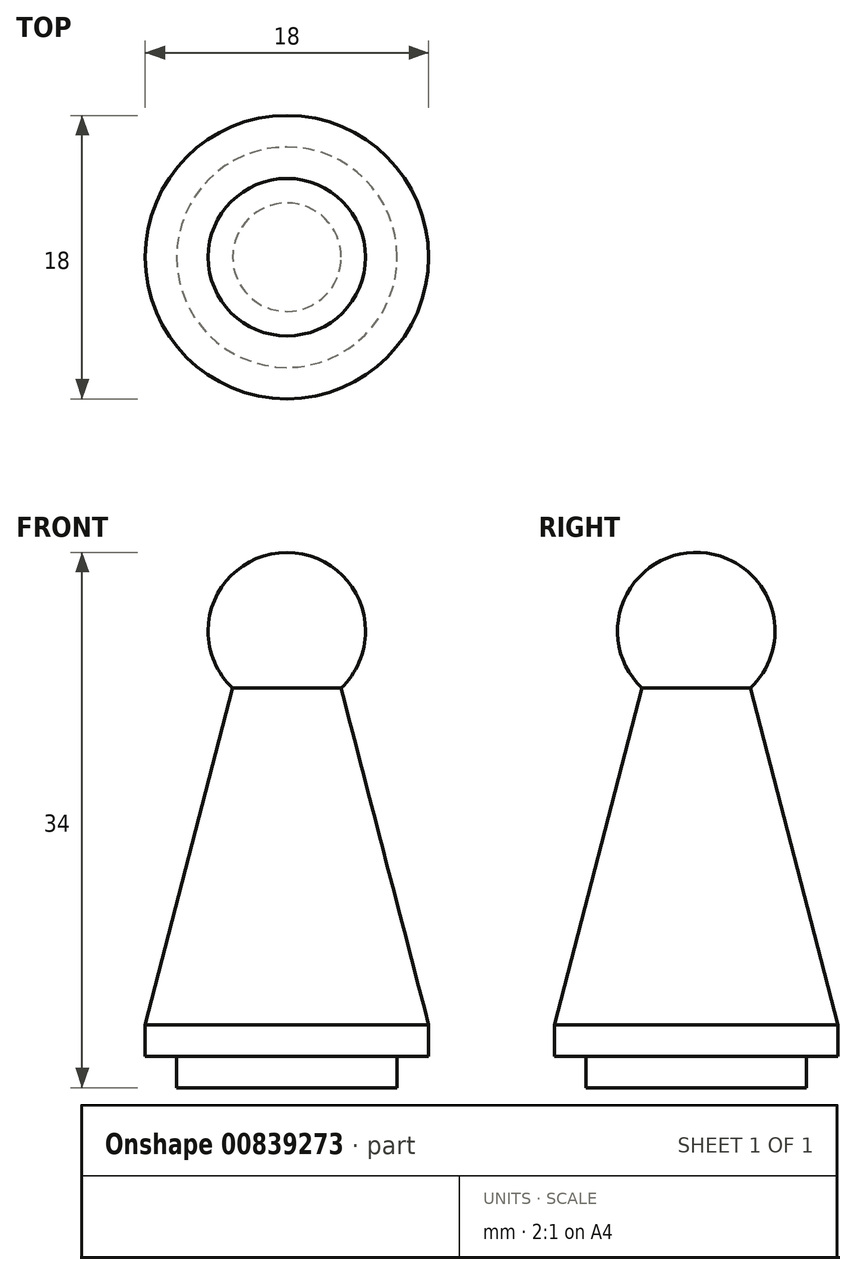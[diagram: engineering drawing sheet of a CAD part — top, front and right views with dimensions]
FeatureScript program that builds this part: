
annotation { "Feature Type Name" : "Feature", "Feature Type Description" : "" }
export const myFeature = defineFeature(function(context is Context, id is Id, definition is map)
    precondition{}
    {
        {
            var Q0;
            Q0=qCreatedBy(makeId("Top.planeOp"),FACE);
            var sketch = newSketch(context, id + "F0", { "sketchPlane" : qUnion([Q0])});
            skCircle(sketch, "E0", {"center": v(0, 0) * mm, "radius": 7 * mm});
            skSolve(sketch);
        }
        {
            var Q0;
            Q0=makeQuery(id+"F0.imprint","IMPRINT",FACE,{"disambiguationData":[TD([[makeQuery(id+"F0.imprint","IMPRINT",EDGE,{"derivedFrom":sQuery(id+"F0.wireOp",EDGE,"E0")}),1.0]])]});
            extrude(context, id + "F1", {"entities" : qUnion([Q0]), "depth" : 2 * mm, "offsetDistance" : 25 * mm});
        }
        {
            var Q0;
            Q0=makeQuery(id+"F1.opExtrude","CAP_FACE",FACE,{"disambiguationData":[OSD([sQuery(id+"F0.wireOp",EDGE,"E0")])],"isStart":false});
            var sketch = newSketch(context, id + "F2", { "sketchPlane" : qUnion([Q0])});
            skCircle(sketch, "E1", {"center": v(0, 0) * mm, "radius": 9 * mm});
            skSolve(sketch);
        }
        {
            var Q0;
            Q0 = qSketchRegion(id + "F2", true);
            extrude(context, id + "F3", {"entities" : qUnion([Q0]), "operationType" : NewBodyOperationType.ADD, "depth" : 2 * mm, "offsetDistance" : 25 * mm});
        }
        {
            var Q0;
            Q0=makeQuery(id+"F3.opExtrude","CAP_FACE",FACE,{"disambiguationData":[OSD([sQuery(id+"F2.wireOp",EDGE,"E1")])],"isStart":false});
            cPlane(context, id + "F4", {"entities" : qUnion([Q0]), "cplaneType" : CPlaneType.OFFSET, "offset" : 25 * mm, "width" : 150 * mm, "height" : 150 * mm});
        }
        {
            var Q0;
            Q0=qCreatedBy(id+"F4.planeOp",FACE);
            var sketch = newSketch(context, id + "F5", { "sketchPlane" : qUnion([Q0])});
            skCircle(sketch, "E2", {"center": v(0, 0) * mm, "radius": 2.5 * mm});
            skSolve(sketch);
        }
        {
            var Q1;
            Q1=makeQuery(id+"F3.opExtrude","CAP_FACE",FACE,{"disambiguationData":[OSD([sQuery(id+"F2.wireOp",EDGE,"E1")])],"isStart":false});
            var Q2;
            Q2=makeQuery(id+"F5.imprint","IMPRINT",FACE,{"disambiguationData":[TD([[makeQuery(id+"F5.imprint","IMPRINT",EDGE,{"derivedFrom":sQuery(id+"F5.wireOp",EDGE,"E2")}),1.0]])]});
            loft(context, id + "F6", {"operationType" : NewBodyOperationType.ADD, "sheetProfilesArray" : [{ "sheetProfileEntities" : qUnion([Q1]) }, { "sheetProfileEntities" : qUnion([Q2]) }]});
        }
        {
            var Q0;
            Q0=makeQuery(id+"F6.opLoft","CAP_FACE",FACE,{"disambiguationData":[OSD([makeQuery(id+"F5.imprint","IMPRINT",FACE,{"disambiguationData":[TD([[makeQuery(id+"F5.imprint","IMPRINT",EDGE,{"derivedFrom":sQuery(id+"F5.wireOp",EDGE,"E2")}),1.0]])]})])],"isStart":true});
            var sketch = newSketch(context, id + "F7", { "sketchPlane" : qUnion([Q0])});
            skCircle(sketch, "E3", {"center": v(0, 0) * mm, "radius": 5 * mm});
            skLineSegment(sketch, "E4", {"start": v(-5, 0) * mm, "end": v(5, 0) * mm});
            skSolve(sketch);
        }
        {
            var Q0;
            {var subQ0=sQuery(id+"F7.wireOp",EDGE,"E4");var subQ1=makeQuery(id+"F6.opLoft","MID_CAP_EDGE",EDGE,{"disambiguationData":[OSD([sQuery(id+"F5.wireOp",EDGE,"E2")])],"capPos":1.0});var subQ2=makeQuery(id+"F7.imprint","INTERSECT",VERTEX,{"disambiguationData":[OD(0.0)],"derivedFrom":[subQ1,subQ0]});Q0=makeQuery(id+"F7.imprint","IMPRINT",FACE,{"disambiguationData":[TD([[makeQuery(id+"F7.imprint","IMPRINT",EDGE,{"disambiguationData":[TD([[subQ2,-1.0]])],"derivedFrom":subQ0}),1.0]])]});}
            var Q1;
            {var subQ0=sQuery(id+"F7.wireOp",EDGE,"E4");var subQ1=sQuery(id+"F7.wireOp",EDGE,"E3");var subQ2=makeQuery(id+"F7.imprint","INTERSECT",VERTEX,{"disambiguationData":[OD(0.0)],"derivedFrom":[subQ1,subQ0]});Q1=makeQuery(id+"F7.imprint","IMPRINT",FACE,{"disambiguationData":[TD([[makeQuery(id+"F7.imprint","IMPRINT",EDGE,{"disambiguationData":[TD([[subQ2,1.0]])],"derivedFrom":subQ1}),1.0]])]});}
            var Q2;
            Q2=sQuery(id+"F7.wireOp",EDGE,"E4");
            revolve(context, id + "F8", {"operationType" : NewBodyOperationType.ADD, "surfaceOperationType" : NewSurfaceOperationType.NEW, "entities" : qUnion([Q0, Q1]), "axis" : qUnion([Q2]), "revolveType" : RevolveType.FULL});
        }
    });
